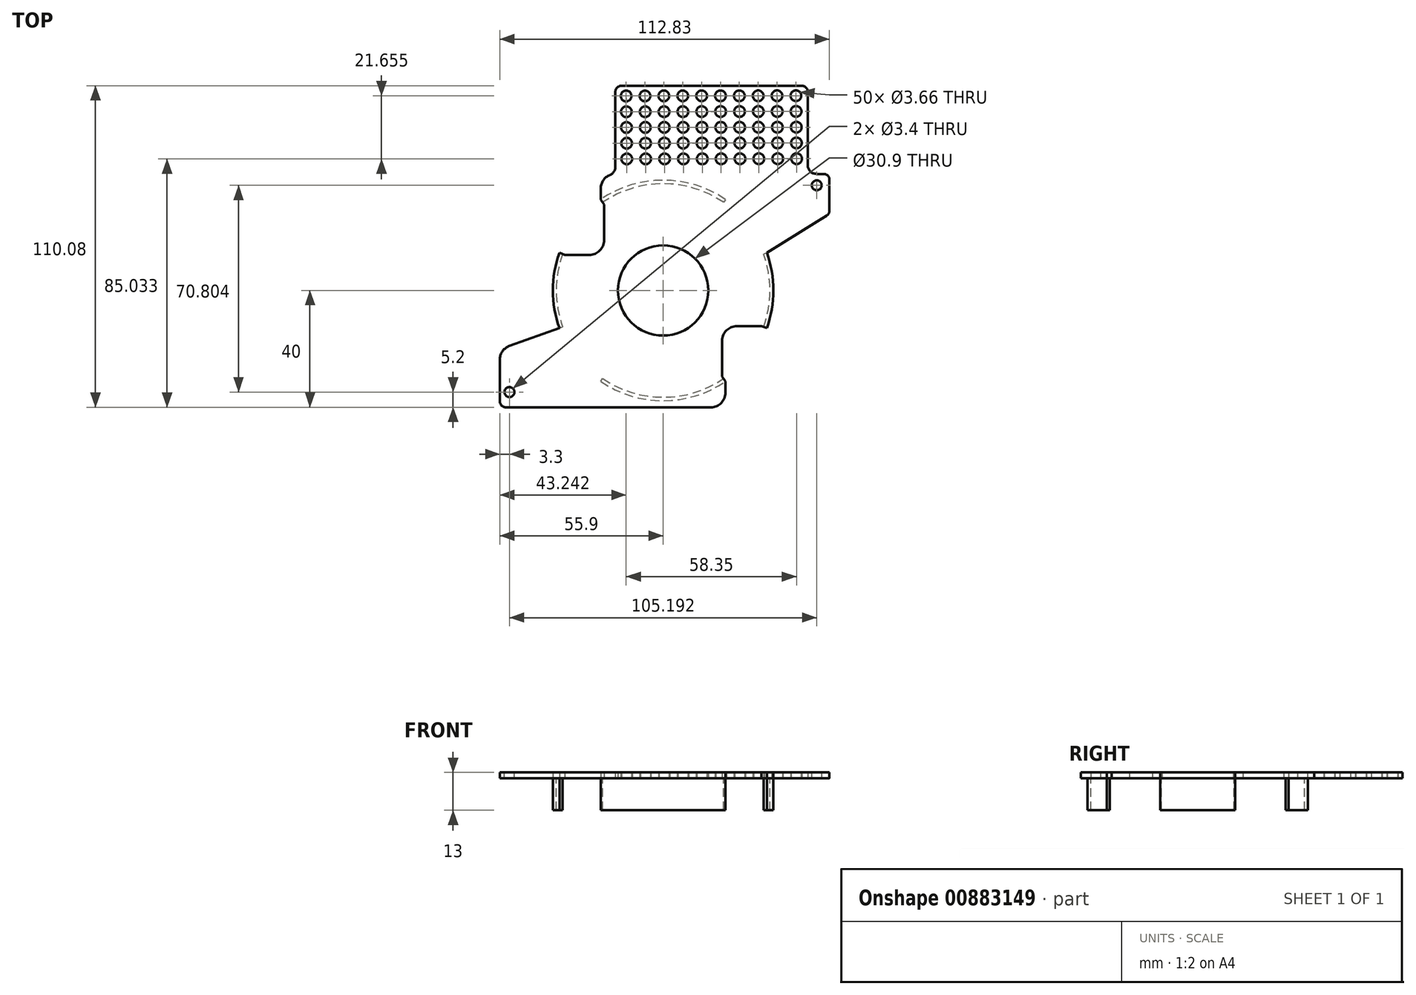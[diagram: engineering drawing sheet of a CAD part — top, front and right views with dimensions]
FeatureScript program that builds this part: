
annotation { "Feature Type Name" : "Feature", "Feature Type Description" : "" }
export const myFeature = defineFeature(function(context is Context, id is Id, definition is map)
    precondition{}
    {
        {
            var Q0;
            Q0=qCreatedBy(makeId("Top.planeOp"),FACE);
            var sketch = newSketch(context, id + "F0", { "sketchPlane" : qUnion([Q0])});
            skLineSegment(sketch, "E0.bottom", {"start": v(52.51, 39.9) * mm, "end": v(54.37, 39.9) * mm});
            skLineSegment(sketch, "E0.top", {"start": v(-53.9, -40) * mm, "end": v(16.35, -40) * mm});
            skLineSegment(sketch, "E1", {"start": v(-52.6, -40) * mm, "end": v(-52.6, -34.8) * mm, "construction": true});
            skLineSegment(sketch, "E2", {"start": v(-52.6, -34.8) * mm, "end": v(-55, -34.8) * mm, "construction": true});
            skLineSegment(sketch, "E3", {"start": v(55, 36) * mm, "end": v(52.6, 36) * mm, "construction": true});
            skLineSegment(sketch, "E4", {"start": v(52.6, 36) * mm, "end": v(52.6, 39.9) * mm, "construction": true});
            skLineSegment(sketch, "E5", {"start": v(-35.5, 12.88) * mm, "end": v(-35.5, 12.88) * mm});
            skLineSegment(sketch, "E6", {"start": v(-35.5, -12.88) * mm, "end": v(-33.61, -12.2) * mm});
            skLineSegment(sketch, "E7", {"start": v(-21.35, 31.14) * mm, "end": v(-20.22, 29.5) * mm});
            skLineSegment(sketch, "E8", {"start": v(21.35, 31.14) * mm, "end": v(20.22, 29.5) * mm});
            skLineSegment(sketch, "E9", {"start": v(35.5, 12.88) * mm, "end": v(33.61, 12.2) * mm});
            skLineSegment(sketch, "E10", {"start": v(35.5, -12.88) * mm, "end": v(33.61, -12.2) * mm});
            skLineSegment(sketch, "E11", {"start": v(21.35, -31.14) * mm, "end": v(20.22, -29.5) * mm});
            skLineSegment(sketch, "E12", {"start": v(-21.35, -31.14) * mm, "end": v(-20.22, -29.5) * mm});
            skLineSegment(sketch, "E13", {"start": v(-33.61, 12.2) * mm, "end": v(-25.22, 12.2) * mm});
            skLineSegment(sketch, "E14", {"start": v(-20.22, 17.2) * mm, "end": v(-20.22, 29.5) * mm});
            skLineSegment(sketch, "E15", {"start": v(33.61, -12.2) * mm, "end": v(25.22, -12.2) * mm});
            skLineSegment(sketch, "E16", {"start": v(20.22, -17.2) * mm, "end": v(20.22, -29.5) * mm});
            skArc(sketch, "E17", {"start": v(-21.35, -31.14) * mm, "mid": v(0, -37.76) * mm, "end": v(21.35, -31.14) * mm});
            skArc(sketch, "E18", {"start": v(-35.5, 12.88) * mm, "mid": v(-37.76, 0) * mm, "end": v(-35.5, -12.88) * mm});
            skLineSegment(sketch, "E19", {"start": v(-35.5, 12.88) * mm, "end": v(-33.61, 12.2) * mm});
            skArc(sketch, "E20.trimOffspring", {"start": v(21.35, 31.14) * mm, "mid": v(0, 37.76) * mm, "end": v(-21.35, 31.14) * mm});
            skArc(sketch, "E21.trimOffspring", {"start": v(35.5, -12.88) * mm, "mid": v(37.76, 0) * mm, "end": v(35.5, 12.88) * mm});
            skLineSegment(sketch, "E22", {"start": v(52.64, 23.56) * mm, "end": v(35.5, 12.88) * mm});
            skLineSegment(sketch, "E23", {"start": v(-52.6, -19) * mm, "end": v(-35.5, -12.88) * mm});
            skLineSegment(sketch, "E24", {"start": v(-21.35, 31.14) * mm, "end": v(-21.35, 34.9) * mm});
            skLineSegment(sketch, "E25", {"start": v(21.35, -31.14) * mm, "end": v(21.35, -35) * mm});
            skLineSegment(sketch, "E26.trimOffspring", {"start": v(-55.9, -23.37) * mm, "end": v(-55.9, -38) * mm});
            skPoint(sketch, "E27.visualSharp", {"position": v(-21.35, 39.9) * mm});
            skArc(sketch, "E27.filletArc", {"start": v(-18.23, 39.54) * mm, "mid": v(-20.5, 37.7) * mm, "end": v(-21.35, 34.9) * mm});
            skPoint(sketch, "E28.visualSharp", {"position": v(21.35, -40) * mm});
            skArc(sketch, "E28.filletArc", {"start": v(16.35, -40) * mm, "mid": v(19.89, -38.54) * mm, "end": v(21.35, -35) * mm});
            skArc(sketch, "E29.filletArc", {"start": v(25.22, -12.2) * mm, "mid": v(21.68, -13.66) * mm, "end": v(20.22, -17.2) * mm});
            skArc(sketch, "E30.filletArc", {"start": v(-25.22, 12.2) * mm, "mid": v(-21.68, 13.66) * mm, "end": v(-20.22, 17.2) * mm});
            skPoint(sketch, "E31.visualSharp", {"position": v(-55, -40) * mm});
            skArc(sketch, "E31.filletArc", {"start": v(-55.9, -38) * mm, "mid": v(-55.31, -39.41) * mm, "end": v(-53.9, -40) * mm});
            skPoint(sketch, "E32.visualSharp", {"position": v(55, 39.9) * mm});
            skArc(sketch, "E33.filletArc", {"start": v(-52.6, -19) * mm, "mid": v(-54.9, -20.69) * mm, "end": v(-55.9, -23.37) * mm});
            skCircle(sketch, "E34", {"center": v(0, 0) * mm, "radius": 15.45 * mm});
            skLineSegment(sketch, "E35.top", {"start": v(-14.35, 70.08) * mm, "end": v(47.51, 70.08) * mm});
            skLineSegment(sketch, "E35.left", {"start": v(-16.35, 42.32) * mm, "end": v(-16.35, 68.08) * mm});
            skLineSegment(sketch, "E35.right", {"start": v(49.51, 42.9) * mm, "end": v(49.51, 68.08) * mm});
            skCircle(sketch, "E36", {"center": v(-12.66, 66.59) * mm, "radius": 1.83 * mm});
            skCircle(sketch, "E37.1.0.0", {"center": v(-6.2, 66.6) * mm, "radius": 1.83 * mm});
            skCircle(sketch, "E37.2.0.0", {"center": v(0.26, 66.61) * mm, "radius": 1.83 * mm});
            skCircle(sketch, "E37.3.0.0", {"center": v(6.72, 66.62) * mm, "radius": 1.83 * mm});
            skCircle(sketch, "E37.4.0.0", {"center": v(13.17, 66.63) * mm, "radius": 1.83 * mm});
            skCircle(sketch, "E37.5.0.0", {"center": v(19.63, 66.64) * mm, "radius": 1.83 * mm});
            skCircle(sketch, "E37.6.0.0", {"center": v(26.09, 66.65) * mm, "radius": 1.83 * mm});
            skCircle(sketch, "E37.7.0.0", {"center": v(32.55, 66.67) * mm, "radius": 1.83 * mm});
            skCircle(sketch, "E37.8.0.0", {"center": v(39, 66.68) * mm, "radius": 1.83 * mm});
            skCircle(sketch, "E37.9.0.0", {"center": v(45.46, 66.69) * mm, "radius": 1.83 * mm});
            skLineSegment(sketch, "E37.direction1", {"start": v(-12.66, 66.59) * mm, "end": v(-6.2, 66.6) * mm, "construction": true});
            skCircle(sketch, "E38.1.0.0", {"center": v(-12.6, 61.2) * mm, "radius": 1.83 * mm});
            skCircle(sketch, "E38.1.0.1", {"center": v(-6.14, 61.21) * mm, "radius": 1.83 * mm});
            skCircle(sketch, "E38.1.0.2", {"center": v(0.32, 61.22) * mm, "radius": 1.83 * mm});
            skCircle(sketch, "E38.1.0.3", {"center": v(6.77, 61.23) * mm, "radius": 1.83 * mm});
            skCircle(sketch, "E38.1.0.4", {"center": v(19.69, 61.25) * mm, "radius": 1.83 * mm});
            skCircle(sketch, "E38.1.0.5", {"center": v(13.23, 61.24) * mm, "radius": 1.83 * mm});
            skCircle(sketch, "E38.1.0.6", {"center": v(26.15, 61.27) * mm, "radius": 1.83 * mm});
            skCircle(sketch, "E38.1.0.7", {"center": v(32.6, 61.28) * mm, "radius": 1.83 * mm});
            skCircle(sketch, "E38.1.0.8", {"center": v(39.06, 61.29) * mm, "radius": 1.83 * mm});
            skCircle(sketch, "E38.1.0.9", {"center": v(45.52, 61.3) * mm, "radius": 1.83 * mm});
            skCircle(sketch, "E38.2.0.0", {"center": v(-12.54, 55.81) * mm, "radius": 1.83 * mm});
            skCircle(sketch, "E38.2.0.1", {"center": v(-6.08, 55.82) * mm, "radius": 1.83 * mm});
            skCircle(sketch, "E38.2.0.2", {"center": v(0.37, 55.83) * mm, "radius": 1.83 * mm});
            skCircle(sketch, "E38.2.0.3", {"center": v(6.83, 55.84) * mm, "radius": 1.83 * mm});
            skCircle(sketch, "E38.2.0.4", {"center": v(19.75, 55.87) * mm, "radius": 1.83 * mm});
            skCircle(sketch, "E38.2.0.5", {"center": v(13.29, 55.85) * mm, "radius": 1.83 * mm});
            skCircle(sketch, "E38.2.0.6", {"center": v(26.2, 55.88) * mm, "radius": 1.83 * mm});
            skCircle(sketch, "E38.2.0.7", {"center": v(32.66, 55.89) * mm, "radius": 1.83 * mm});
            skCircle(sketch, "E38.2.0.8", {"center": v(39.12, 55.9) * mm, "radius": 1.83 * mm});
            skCircle(sketch, "E38.2.0.9", {"center": v(45.58, 55.9) * mm, "radius": 1.83 * mm});
            skCircle(sketch, "E38.3.0.0", {"center": v(-12.48, 50.42) * mm, "radius": 1.83 * mm});
            skCircle(sketch, "E38.3.0.1", {"center": v(-6.03, 50.43) * mm, "radius": 1.83 * mm});
            skCircle(sketch, "E38.3.0.2", {"center": v(0.43, 50.44) * mm, "radius": 1.83 * mm});
            skCircle(sketch, "E38.3.0.3", {"center": v(6.89, 50.45) * mm, "radius": 1.83 * mm});
            skCircle(sketch, "E38.3.0.4", {"center": v(19.8, 50.48) * mm, "radius": 1.83 * mm});
            skCircle(sketch, "E38.3.0.5", {"center": v(13.35, 50.47) * mm, "radius": 1.83 * mm});
            skCircle(sketch, "E38.3.0.6", {"center": v(26.26, 50.49) * mm, "radius": 1.83 * mm});
            skCircle(sketch, "E38.3.0.7", {"center": v(32.72, 50.5) * mm, "radius": 1.83 * mm});
            skCircle(sketch, "E38.3.0.8", {"center": v(39.18, 50.5) * mm, "radius": 1.83 * mm});
            skCircle(sketch, "E38.3.0.9", {"center": v(45.64, 50.52) * mm, "radius": 1.83 * mm});
            skCircle(sketch, "E38.4.0.0", {"center": v(-12.43, 45.03) * mm, "radius": 1.83 * mm});
            skCircle(sketch, "E38.4.0.1", {"center": v(-5.97, 45.04) * mm, "radius": 1.83 * mm});
            skCircle(sketch, "E38.4.0.2", {"center": v(0.49, 45.05) * mm, "radius": 1.83 * mm});
            skCircle(sketch, "E38.4.0.3", {"center": v(6.95, 45.07) * mm, "radius": 1.83 * mm});
            skCircle(sketch, "E38.4.0.4", {"center": v(19.86, 45.09) * mm, "radius": 1.83 * mm});
            skCircle(sketch, "E38.4.0.5", {"center": v(13.4, 45.08) * mm, "radius": 1.83 * mm});
            skCircle(sketch, "E38.4.0.6", {"center": v(26.32, 45.1) * mm, "radius": 1.83 * mm});
            skCircle(sketch, "E38.4.0.7", {"center": v(32.78, 45.1) * mm, "radius": 1.83 * mm});
            skCircle(sketch, "E38.4.0.8", {"center": v(39.24, 45.12) * mm, "radius": 1.83 * mm});
            skCircle(sketch, "E38.4.0.9", {"center": v(45.7, 45.13) * mm, "radius": 1.83 * mm});
            skLineSegment(sketch, "E38.direction1", {"start": v(-12.66, 66.59) * mm, "end": v(-12.6, 61.2) * mm, "construction": true});
            skLineSegment(sketch, "E39", {"start": v(-52.6, -34.8) * mm, "end": v(52.6, 36) * mm, "construction": true});
            skArc(sketch, "E40.filletArc", {"start": v(49.51, 42.9) * mm, "mid": v(50.4, 40.78) * mm, "end": v(52.51, 39.9) * mm});
            skPoint(sketch, "E41.visualSharp", {"position": v(-16.35, 39.9) * mm});
            skArc(sketch, "E41.filletArc", {"start": v(-18.23, 39.54) * mm, "mid": v(-16.86, 40.64) * mm, "end": v(-16.35, 42.32) * mm});
            skLineSegment(sketch, "E42", {"start": v(54.93, 39.9) * mm, "end": v(55, 39.9) * mm});
            skLineSegment(sketch, "E43", {"start": v(56.93, 37.9) * mm, "end": v(56.93, 27.3) * mm});
            skLineSegment(sketch, "E44", {"start": v(55.97, 25.6) * mm, "end": v(52.64, 23.56) * mm});
            skLineSegment(sketch, "E45", {"start": v(54.37, 39.9) * mm, "end": v(55, 39.9) * mm});
            skLineSegment(sketch, "E46", {"start": v(55, 36) * mm, "end": v(56.93, 36) * mm, "construction": true});
            skPoint(sketch, "E47.visualSharp", {"position": v(56.93, 39.9) * mm});
            skArc(sketch, "E47.filletArc", {"start": v(56.93, 37.9) * mm, "mid": v(56.34, 39.32) * mm, "end": v(54.93, 39.9) * mm});
            skPoint(sketch, "E48.visualSharp", {"position": v(56.93, 26.18) * mm});
            skArc(sketch, "E48.filletArc", {"start": v(55.97, 25.6) * mm, "mid": v(56.67, 26.33) * mm, "end": v(56.93, 27.3) * mm});
            skPoint(sketch, "E49.visualSharp", {"position": v(49.51, 70.08) * mm});
            skArc(sketch, "E49.filletArc", {"start": v(49.51, 68.08) * mm, "mid": v(48.93, 69.5) * mm, "end": v(47.51, 70.08) * mm});
            skPoint(sketch, "E50.visualSharp", {"position": v(-16.35, 70.08) * mm});
            skArc(sketch, "E50.filletArc", {"start": v(-14.35, 70.08) * mm, "mid": v(-15.77, 69.5) * mm, "end": v(-16.35, 68.08) * mm});
            skArc(sketch, "E51.0", {"start": v(-20.67, -30.15) * mm, "mid": v(0, -36.56) * mm, "end": v(20.67, -30.15) * mm});
            skArc(sketch, "E52.0", {"start": v(20.67, 30.15) * mm, "mid": v(0, 36.56) * mm, "end": v(-20.67, 30.15) * mm});
            skArc(sketch, "E53.0", {"start": v(34.36, -12.47) * mm, "mid": v(36.56, 0) * mm, "end": v(34.36, 12.47) * mm});
            skArc(sketch, "E54.0", {"start": v(-34.36, 12.47) * mm, "mid": v(-36.56, 0) * mm, "end": v(-34.36, -12.47) * mm});
            skSolve(sketch);
        }
        {
            var Q0;
            Q0=makeQuery(id+"F0.imprint","IMPRINT",FACE,{"disambiguationData":[TD([[makeQuery(id+"F0.imprint","IMPRINT",EDGE,{"derivedFrom":sQuery(id+"F0.wireOp",EDGE,"E11")}),1.0]])]});
            var Q1;
            Q1=makeQuery(id+"F0.imprint","IMPRINT",FACE,{"disambiguationData":[TD([[makeQuery(id+"F0.imprint","IMPRINT",EDGE,{"derivedFrom":sQuery(id+"F0.wireOp",EDGE,"E6")}),1.0]])]});
            var Q2;
            Q2=makeQuery(id+"F0.imprint","IMPRINT",FACE,{"disambiguationData":[TD([[makeQuery(id+"F0.imprint","IMPRINT",EDGE,{"derivedFrom":sQuery(id+"F0.wireOp",EDGE,"E9")}),1.0]])]});
            var Q3;
            Q3=makeQuery(id+"F0.imprint","IMPRINT",FACE,{"disambiguationData":[TD([[makeQuery(id+"F0.imprint","IMPRINT",EDGE,{"derivedFrom":sQuery(id+"F0.wireOp",EDGE,"E7")}),1.0]])]});
            extrude(context, id + "F1", {"entities" : qUnion([Q0, Q1, Q2, Q3]), "depth" : -11 * mm, "offsetDistance" : 25 * mm});
        }
        {
            var Q0;
            Q0 = qSketchRegion(id + "F0", true);
            extrude(context, id + "F2", {"entities" : qUnion([Q0]), "depth" : 2 * mm, "offsetDistance" : 25 * mm});
        }
        {
            var Q0;
            Q0=sQuery(id+"F0.wireOp",VERTEX,"E3.end");
            var Q1;
            Q1=sQuery(id+"F0.wireOp",VERTEX,"E1.end");
            var Q2;
            Q2=makeQuery(id+"F2.opExtrude","SWEPT_BODY",BODY,{"disambiguationData":[OSD([sQuery(id+"F0.wireOp",EDGE,"E0.bottom"),sQuery(id+"F0.wireOp",EDGE,"E0.top"),sQuery(id+"F0.wireOp",EDGE,"E0.right"),sQuery(id+"F0.wireOp",EDGE,"E7"),sQuery(id+"F0.wireOp",EDGE,"E10"),sQuery(id+"F0.wireOp",EDGE,"E11"),sQuery(id+"F0.wireOp",EDGE,"E13"),sQuery(id+"F0.wireOp",EDGE,"E14"),sQuery(id+"F0.wireOp",EDGE,"E15"),sQuery(id+"F0.wireOp",EDGE,"E16"),sQuery(id+"F0.wireOp",EDGE,"E18"),sQuery(id+"F0.wireOp",EDGE,"E19"),sQuery(id+"F0.wireOp",EDGE,"E21.trimOffspring"),sQuery(id+"F0.wireOp",EDGE,"E22"),sQuery(id+"F0.wireOp",EDGE,"E23"),sQuery(id+"F0.wireOp",EDGE,"E24"),sQuery(id+"F0.wireOp",EDGE,"E25"),sQuery(id+"F0.wireOp",EDGE,"E26.trimOffspring"),sQuery(id+"F0.wireOp",EDGE,"E27.filletArc"),sQuery(id+"F0.wireOp",EDGE,"E28.filletArc"),sQuery(id+"F0.wireOp",EDGE,"E29.filletArc"),sQuery(id+"F0.wireOp",EDGE,"E30.filletArc"),sQuery(id+"F0.wireOp",EDGE,"E31.filletArc"),sQuery(id+"F0.wireOp",EDGE,"E32.filletArc"),sQuery(id+"F0.wireOp",EDGE,"E33.filletArc"),sQuery(id+"F0.wireOp",EDGE,"a0fa5af9-6cd3-49f4-b36d-8b19806cc85a.filletArc"),sQuery(id+"F0.wireOp",EDGE,"E34"),sQuery(id+"F0.wireOp",EDGE,"E35.top"),sQuery(id+"F0.wireOp",EDGE,"E35.left"),sQuery(id+"F0.wireOp",EDGE,"E35.right"),sQuery(id+"F0.wireOp",EDGE,"E36"),sQuery(id+"F0.wireOp",EDGE,"E37.1.0.0"),sQuery(id+"F0.wireOp",EDGE,"E37.2.0.0"),sQuery(id+"F0.wireOp",EDGE,"E37.3.0.0"),sQuery(id+"F0.wireOp",EDGE,"E37.4.0.0"),sQuery(id+"F0.wireOp",EDGE,"E37.5.0.0"),sQuery(id+"F0.wireOp",EDGE,"E37.6.0.0"),sQuery(id+"F0.wireOp",EDGE,"E37.7.0.0"),sQuery(id+"F0.wireOp",EDGE,"E37.8.0.0"),sQuery(id+"F0.wireOp",EDGE,"E37.9.0.0"),sQuery(id+"F0.wireOp",EDGE,"E38.1.0.0"),sQuery(id+"F0.wireOp",EDGE,"E38.1.0.1"),sQuery(id+"F0.wireOp",EDGE,"E38.1.0.2"),sQuery(id+"F0.wireOp",EDGE,"E38.1.0.3"),sQuery(id+"F0.wireOp",EDGE,"E38.1.0.4"),sQuery(id+"F0.wireOp",EDGE,"E38.1.0.5"),sQuery(id+"F0.wireOp",EDGE,"E38.1.0.6"),sQuery(id+"F0.wireOp",EDGE,"E38.1.0.7"),sQuery(id+"F0.wireOp",EDGE,"E38.1.0.8"),sQuery(id+"F0.wireOp",EDGE,"E38.1.0.9"),sQuery(id+"F0.wireOp",EDGE,"E38.2.0.0"),sQuery(id+"F0.wireOp",EDGE,"E38.2.0.1"),sQuery(id+"F0.wireOp",EDGE,"E38.2.0.2"),sQuery(id+"F0.wireOp",EDGE,"E38.2.0.3"),sQuery(id+"F0.wireOp",EDGE,"E38.2.0.4"),sQuery(id+"F0.wireOp",EDGE,"E38.2.0.5"),sQuery(id+"F0.wireOp",EDGE,"E38.2.0.6"),sQuery(id+"F0.wireOp",EDGE,"E38.2.0.7"),sQuery(id+"F0.wireOp",EDGE,"E38.2.0.8"),sQuery(id+"F0.wireOp",EDGE,"E38.2.0.9"),sQuery(id+"F0.wireOp",EDGE,"E38.3.0.0"),sQuery(id+"F0.wireOp",EDGE,"E38.3.0.1"),sQuery(id+"F0.wireOp",EDGE,"E38.3.0.2"),sQuery(id+"F0.wireOp",EDGE,"E38.3.0.3"),sQuery(id+"F0.wireOp",EDGE,"E38.3.0.4"),sQuery(id+"F0.wireOp",EDGE,"E38.3.0.5"),sQuery(id+"F0.wireOp",EDGE,"E38.3.0.6"),sQuery(id+"F0.wireOp",EDGE,"E38.3.0.7"),sQuery(id+"F0.wireOp",EDGE,"E38.3.0.8"),sQuery(id+"F0.wireOp",EDGE,"E38.3.0.9"),sQuery(id+"F0.wireOp",EDGE,"E38.4.0.0"),sQuery(id+"F0.wireOp",EDGE,"E38.4.0.1"),sQuery(id+"F0.wireOp",EDGE,"E38.4.0.2"),sQuery(id+"F0.wireOp",EDGE,"E38.4.0.3"),sQuery(id+"F0.wireOp",EDGE,"E38.4.0.4"),sQuery(id+"F0.wireOp",EDGE,"E38.4.0.5"),sQuery(id+"F0.wireOp",EDGE,"E38.4.0.6"),sQuery(id+"F0.wireOp",EDGE,"E38.4.0.7"),sQuery(id+"F0.wireOp",EDGE,"E38.4.0.8"),sQuery(id+"F0.wireOp",EDGE,"E38.4.0.9")])]});
            hole(context, id + "F3", {"style" : HoleStyle.SIMPLE, "endStyle" : HoleEndStyle.THROUGH, "oppositeDirection" : true, "standardTappedOrClearance" : lookupTablePath({ "fit" : "Normal", "standard" : "ISO", "size" : "M3", "type" : "Clearance" }), "standardBlindInLast" : lookupTablePath({ "fit" : "Normal", "standard" : "ISO", "engagement" : "75%", "pitch" : "0.5 mm", "size" : "M3", "type" : "Clearance & tapped" }), "holeDiameter" : 3.4 * mm, "majorDiameter" : 3 * mm, "isTappedThrough" : true, "tappedDepth" : 12 * mm, "tapClearance" : 3, "locations" : qUnion([Q0, Q1]), "scope" : qUnion([Q2])});
        }
    });
